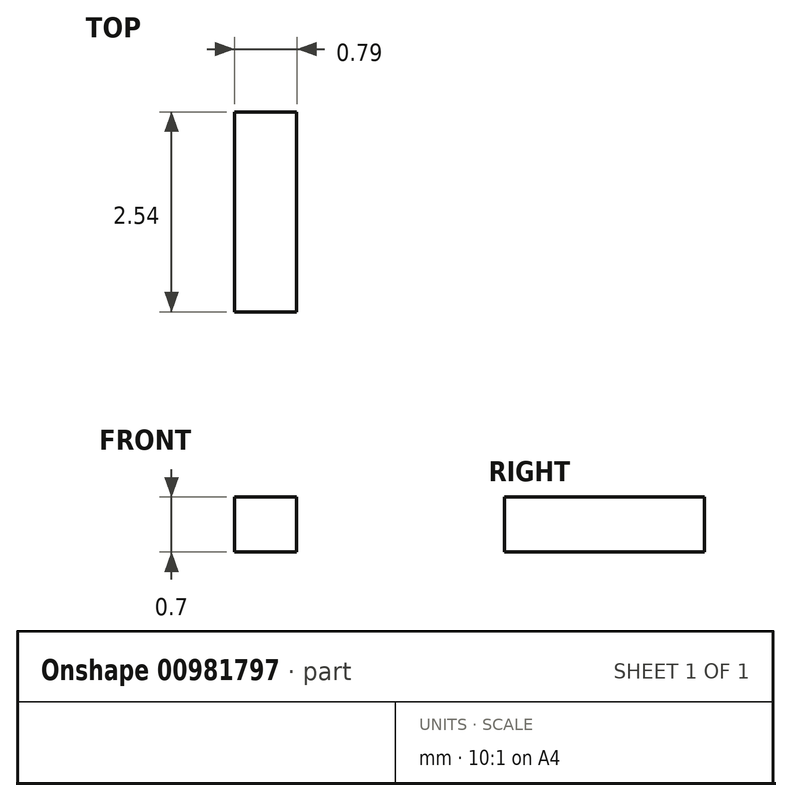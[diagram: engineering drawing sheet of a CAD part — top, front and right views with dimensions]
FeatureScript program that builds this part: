
annotation { "Feature Type Name" : "Feature", "Feature Type Description" : "" }
export const myFeature = defineFeature(function(context is Context, id is Id, definition is map)
    precondition{}
    {
        {
            var Q0;
            Q0=qCreatedBy(makeId("Front.planeOp"),FACE);
            var sketch = newSketch(context, id + "F0", { "sketchPlane" : qUnion([Q0])});
            skLineSegment(sketch, "E0.bottom", {"start": v(-6.9, 0.31) * mm, "end": v(-6.11, 0.31) * mm});
            skLineSegment(sketch, "E0.top", {"start": v(-6.9, 1) * mm, "end": v(-6.11, 1) * mm});
            skLineSegment(sketch, "E0.left", {"start": v(-6.9, 0.31) * mm, "end": v(-6.9, 1) * mm});
            skLineSegment(sketch, "E0.right", {"start": v(-6.11, 0.31) * mm, "end": v(-6.11, 1) * mm});
            skSolve(sketch);
        }
        {
            var Q0;
            Q0=makeQuery(id+"F0.imprint","IMPRINT",FACE,{"disambiguationData":[TD([[makeQuery(id+"F0.imprint","IMPRINT",EDGE,{"derivedFrom":sQuery(id+"F0.wireOp",EDGE,"E0.bottom")}),1.0]])]});
            extrude(context, id + "F1", {"entities" : qUnion([Q0]), "depth" : 2.54 * mm, "offsetDistance" : 25.4 * mm});
        }
    });
